# Revit family: equip-water-cooler-elkay-ez-ada
name_source: partatom
category: Plumbing Fixtures
units: mm (PartAtom-declared; Revit-internal decimal feet)

## family parameters
Always vertical = Yes
Cut with Voids When Loaded = No
OmniClass Number = 23.45.00.00
OmniClass Title = Sanitary, Laundry, and Cleaning Equipment
Part Type = Normal
Room Calculation Point = No
Round Connector Dimension = Use Radius
Shared = No
Work Plane-Based = No

## types (18) — shared parameters
Basin Material = Metal - Steel - Stainless - Chrome
CW Connection = Yes
Cooler Bottom = 1' - 0 1/2"
Cooler Depth = 1' - 7"
Cooler Height = 1' - 8 3/8"
Cooler Rear Panel Depth = 0' - 6 43/256"
Cooler Separation = 0' - 0"
Cooler Width = 1' - 6 57/64"
Description = EZ ADA
Dispenser ADA Height = 2' - 4 19/32"
Dispenser Depth = 0' - 8 25/64"
Floor to Bottom = 1' - 0 1/2"
HW Connection = No
Manufacturer = Elkay
Orifice Height = 2' - 8 7/8"
Orifice to Rim = 0' - 1 9/16"
Panel Material = Metal - Steel - Stainless - Color 3
Rim Height = 2' - 7 5/16"
Rim to Dispenser = 0' - 4 9/32"
Rim to Top of Bottom Panel = 0' - 5 9/32"
Specification = http://www.elkayusa.com
TOP SKETCH = Yes
Top Panel Material = Metal - Steel - Stainless - Color 2
Type = Single
URL = http://www.elkay.com
Vent Connection = No
Version = 1.0.0.0
Waste Connection = Yes
Water Service Flow = 0 GPM
Water Service Size Radius = 0' - 0 1/4"

## per-type parameters (varying)
| type | Activation | Bubbler | Filter | Frost Resist | Glass Filter | Louver Screens | Model | Other Features | Refrigerated | Volts/Hertz |
| EZO 8* | Sensor | Flexi-Guard | See LZ | - |  | - | EZO8* |  | Yes | 115V/60Hz |
| EZ SD* | Pushbars | Flexi-Guard | See LZ |  | See EZSDF | - | EZSD* |  | No | 150V/60Hz |
| EZ SD*F | Pushbars | Flexi-Guard | Accessory Ordered Separately |  | Factory Prepped (Order GF Separately) | Yes | EZSD*F |  | No | 115v/60Hz |
| EZO VR8* | Sensor | VR Bubbler | Accessory Ordered Separately | - |  | - | EZOVR8* |  | Yes | 115V/60Hz |
| EZ SVR8* | Pushbar | VR Bubbler | See LZ | - | - | - | EZSVR8* |  | Yes | 115V/60Hz |
| EZ S8*F | Pushbars | Flexi-Guard | See LZ |  | Factory Prepped (Order GF Separately) |  | EZS8*F |  | Yes | 115V/60Hz |
| EZ S8* | Pushbars | Flexi-Guard | See LZ |  | see EZS8F |  | EZS8* |  | Yes | 115V/60Hz |
| EZ S4* | Pushbars | Flexi-Guard | Accessory Ordered Separately |  | see EZS4F |  | EZS4* |  | Yes | 115V/60Hz |
| EZ S4*F | Pushbars | Flexi-Guard | See LZ |  | Factory Prepped (Order GF Separately) |  | EZS4*F |  | Yes | 115V/60Hz |
| EZO 4* | Sensor | Flexi-Guard | Accessory Ordered Separately |  |  |  | EZO4* |  | Yes | 115V/60Hz |
| EZ SVRD* | Pushbars | VR Bubbler | Accessory Ordered Separately | - | - | - | EZSVRD* |  | No | 115V/60Hz |
| EZO D* | Sensor | Flexi-Guard | See LZ | - |  | - | EZOD* |  | No | 115V/60Hz |
| LZO 8* | Sensor | Flexi-Guard | EWF 172 | - |  | - | LZO8* | VFM | Yes | 115V/60Hz |
| LZO D* | Sensor | Flexi-Guard | EWF 172 | - |  | - | LZOD* | VFM | No | 115V/60Hz |
| LZ S8* | Pushbars | Flexi-Guard | EWF 172 |  | see LZS8F |  | LZS8* |  | Yes | 115V/60Hz |
| LZ S8*F | Pushbars | Flexi-Guard | EWF 172 |  | Factory Prepped (Order GF Separately) |  | LZS8*F |  | Yes | 115V/60Hz |
| LZ SVR8* | Pushbar | VR Bubbler | EWF 172 | - | - | - | LZSVR8* |  | Yes | 115V/60Hz |
| LZ SD* | Pushbars | Flexi-Guard | EWF 172 |  | -- | - | LZSD* | EWF 172 | No | 150V/60Hz |

## geometry (parser evidence)
native form markers: Extrusion x1, Sweep x9
no freeform markers — native parametric forms only
